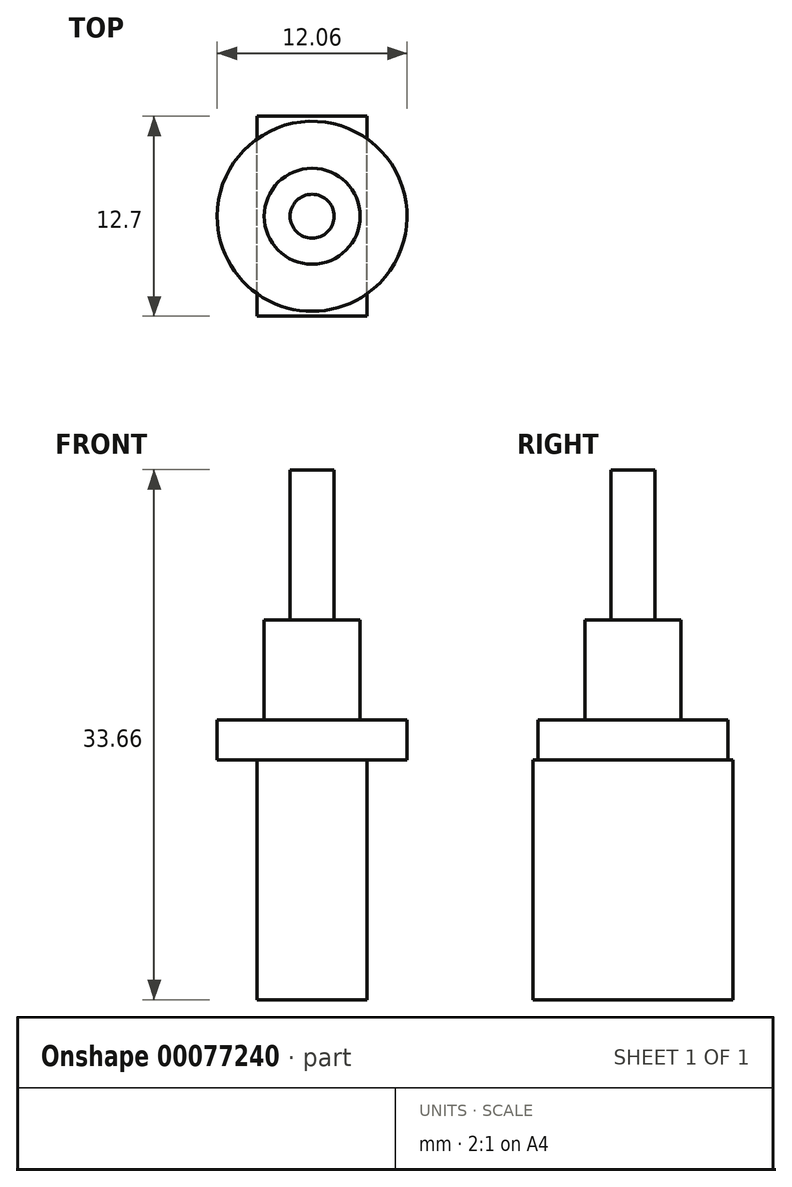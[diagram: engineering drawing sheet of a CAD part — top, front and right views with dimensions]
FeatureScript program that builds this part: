
annotation { "Feature Type Name" : "Feature", "Feature Type Description" : "" }
export const myFeature = defineFeature(function(context is Context, id is Id, definition is map)
    precondition{}
    {
        {
            var Q0;
            Q0=qCreatedBy(makeId("Top.planeOp"),FACE);
            var sketch = newSketch(context, id + "F0", { "sketchPlane" : qUnion([Q0])});
            skCircle(sketch, "E0", {"center": v(0, 0) * mm, "radius": 3.05 * mm});
            skSolve(sketch);
        }
        {
            var Q0;
            Q0=makeQuery(id+"F0.imprint","IMPRINT",FACE,{"disambiguationData":[TD([[makeQuery(id+"F0.imprint","IMPRINT",EDGE,{"derivedFrom":sQuery(id+"F0.wireOp",EDGE,"E0")}),1.0]])]});
            extrude(context, id + "F1", {"entities" : qUnion([Q0]), "depth" : 6.35 * mm});
        }
        {
            var Q0;
            Q0=makeQuery(id+"F1.opExtrude","CAP_FACE",FACE,{"disambiguationData":[OSD([sQuery(id+"F0.wireOp",EDGE,"E0")])],"isStart":true});
            var sketch = newSketch(context, id + "F2", { "sketchPlane" : qUnion([Q0])});
            skCircle(sketch, "E1", {"center": v(0, 0) * mm, "radius": 6.03 * mm});
            skSolve(sketch);
        }
        {
            var Q0;
            Q0=makeQuery(id+"F2.imprint","IMPRINT",FACE,{"disambiguationData":[TD([[makeQuery(id+"F2.imprint","IMPRINT",EDGE,{"derivedFrom":sQuery(id+"F2.wireOp",EDGE,"E1")}),1.0]])]});
            var Q1;
            Q1=makeQuery(id+"F2.imprint","IMPRINT",FACE,{"disambiguationData":[TD([[makeQuery(id+"F2.imprint","IMPRINT",EDGE,{"derivedFrom":makeQuery(id+"F1.opExtrude","CAP_EDGE",EDGE,{"disambiguationData":[OSD([sQuery(id+"F0.wireOp",EDGE,"E0")])],"isStart":true})}),-1.0]])]});
            extrude(context, id + "F3", {"entities" : qUnion([Q0, Q1]), "operationType" : NewBodyOperationType.ADD, "depth" : 2.54 * mm});
        }
        {
            var Q0;
            Q0=makeQuery(id+"F3.opExtrude","CAP_FACE",FACE,{"disambiguationData":[OSD([sQuery(id+"F2.wireOp",EDGE,"E1")])],"isStart":false});
            var sketch = newSketch(context, id + "F4", { "sketchPlane" : qUnion([Q0])});
            skLineSegment(sketch, "E2.bottom", {"start": v(-3.5, 6.35) * mm, "end": v(3.5, 6.35) * mm});
            skLineSegment(sketch, "E2.top", {"start": v(-3.5, -6.35) * mm, "end": v(3.5, -6.35) * mm});
            skLineSegment(sketch, "E2.left", {"start": v(-3.5, 6.35) * mm, "end": v(-3.5, -6.35) * mm});
            skLineSegment(sketch, "E2.right", {"start": v(3.5, 6.35) * mm, "end": v(3.5, -6.35) * mm});
            skLineSegment(sketch, "E3", {"start": v(-3.5, 6.35) * mm, "end": v(3.5, -6.35) * mm});
            skSolve(sketch);
        }
        {
            var Q0;
            Q0 = qSketchRegion(id + "F4", true);
            extrude(context, id + "F5", {"entities" : qUnion([Q0]), "operationType" : NewBodyOperationType.ADD, "depth" : 15.24 * mm});
        }
        {
            var Q0;
            Q0=makeQuery(id+"F1.opExtrude","CAP_FACE",FACE,{"disambiguationData":[OSD([sQuery(id+"F0.wireOp",EDGE,"E0")])],"isStart":false});
            var sketch = newSketch(context, id + "F6", { "sketchPlane" : qUnion([Q0])});
            skCircle(sketch, "E4", {"center": v(0, 0) * mm, "radius": 1.4 * mm});
            skSolve(sketch);
        }
        {
            var Q0;
            Q0 = qSketchRegion(id + "F6", true);
            extrude(context, id + "F7", {"entities" : qUnion([Q0]), "operationType" : NewBodyOperationType.ADD, "depth" : 9.52 * mm});
        }
    });
